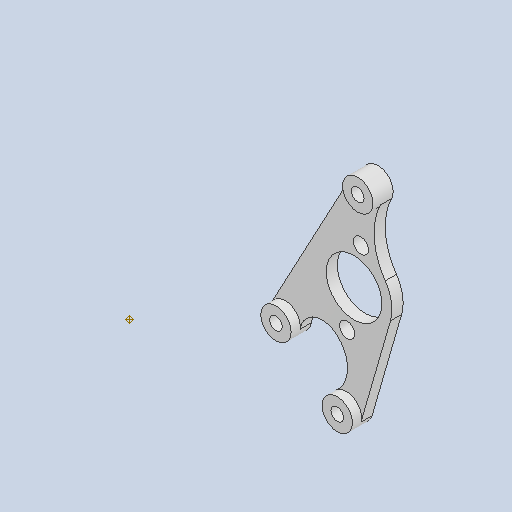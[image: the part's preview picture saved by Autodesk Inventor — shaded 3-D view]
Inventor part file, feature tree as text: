
AUTODESK INVENTOR PART (.ipt)
format: ipt  version: 2023 (Build 270158030, 158C)  size: 149,504 bytes
history: native  units: mm
features: extrude x2, sketch x1
ambient origin geometry x8: Origin, YZ Plane, XZ Plane, XY Plane, X Axis, Y Axis, Z Axis, Center Point
bodies: Body1 (feature_tree)
feature tree (3):
  sketch  "Sketch1"  dims[d61=11.0mm d62=3.0mm d63=8.0mm d64=8.0mm d65=5.5mm d66=2.0mm d67=3.0mm d68=6.0mm d69=6.0mm d70=6.0mm d71=6.3mm d72=12.4mm d73=1.5mm d74=2.2mm d75=0.0mm d76=4.0mm d77=0.0mm d78=0.5mm d79=0.872665mm d80=0.5mm d81=0.872665mm]
  extrude  "Extrusion5"  Depth=4.0mm TaperAngle=0.0deg
  extrude  "Extrusion6"  Depth=4.0mm
